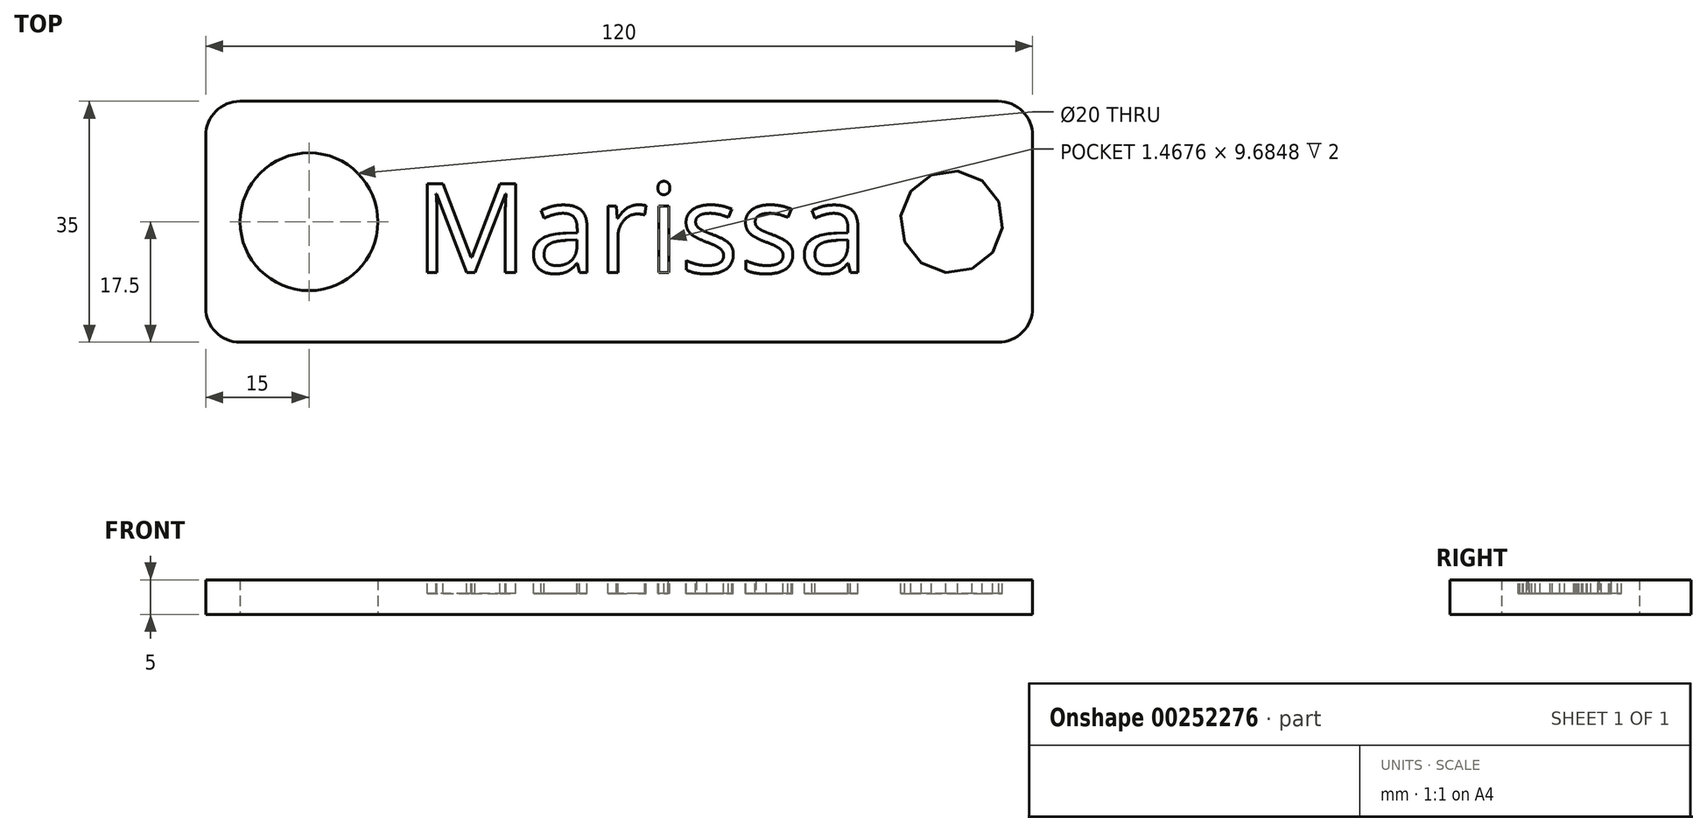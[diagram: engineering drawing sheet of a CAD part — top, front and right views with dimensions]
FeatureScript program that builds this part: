
annotation { "Feature Type Name" : "Feature", "Feature Type Description" : "" }
export const myFeature = defineFeature(function(context is Context, id is Id, definition is map)
    precondition{}
    {
        {
            var Q0;
            Q0=qCreatedBy(makeId("Top.planeOp"),FACE);
            var sketch = newSketch(context, id + "F0", { "sketchPlane" : qUnion([Q0])});
            skPoint(sketch, "E0.middle", {"position": v(0, 0) * mm});
            skLineSegment(sketch, "E1.bottom", {"start": v(60, -17.5) * mm, "end": v(-60, -17.5) * mm});
            skLineSegment(sketch, "E1.top", {"start": v(60, 17.5) * mm, "end": v(-60, 17.5) * mm});
            skLineSegment(sketch, "E1.left", {"start": v(60, -17.5) * mm, "end": v(60, 17.5) * mm});
            skLineSegment(sketch, "E1.right", {"start": v(-60, -17.5) * mm, "end": v(-60, 17.5) * mm});
            skCircle(sketch, "E2", {"center": v(-45, 0) * mm, "radius": 10 * mm});
            skSolve(sketch);
        }
        {
            var Q0;
            Q0=makeQuery(id+"F0.imprint","IMPRINT",FACE,{"disambiguationData":[TD([[makeQuery(id+"F0.imprint","IMPRINT",EDGE,{"derivedFrom":sQuery(id+"F0.wireOp",EDGE,"E1.bottom")}),-1.0]])]});
            extrude(context, id + "F1", {"entities" : qUnion([Q0]), "depth" : 5 * mm});
        }
        {
            var Q0;
            Q0=makeQuery(id+"F1.opExtrude","SWEPT_EDGE",EDGE,{"disambiguationData":[OSD([sQuery(id+"F0.wireOp",EDGE,"E1.bottom"),sQuery(id+"F0.wireOp",EDGE,"E1.right")])]});
            var Q1;
            Q1=makeQuery(id+"F1.opExtrude","SWEPT_EDGE",EDGE,{"disambiguationData":[OSD([sQuery(id+"F0.wireOp",EDGE,"E1.bottom"),sQuery(id+"F0.wireOp",EDGE,"E1.left")])]});
            var Q2;
            Q2=makeQuery(id+"F1.opExtrude","SWEPT_EDGE",EDGE,{"disambiguationData":[OSD([sQuery(id+"F0.wireOp",EDGE,"E1.top"),sQuery(id+"F0.wireOp",EDGE,"E1.left")])]});
            var Q3;
            Q3=makeQuery(id+"F1.opExtrude","SWEPT_EDGE",EDGE,{"disambiguationData":[OSD([sQuery(id+"F0.wireOp",EDGE,"E1.top"),sQuery(id+"F0.wireOp",EDGE,"E1.right")])]});
            fillet(context, id + "F2", {"entities" : qUnion([Q0, Q1, Q2, Q3]), "radius" : 5 * mm, "tangentPropagation" : true, "allowEdgeOverflow" : false});
        }
        {
            var Q0;
            Q0=makeQuery(id+"F1.opExtrude","CAP_FACE",FACE,{"disambiguationData":[OSD([sQuery(id+"F0.wireOp",EDGE,"E1.bottom"),sQuery(id+"F0.wireOp",EDGE,"E1.top"),sQuery(id+"F0.wireOp",EDGE,"E1.left"),sQuery(id+"F0.wireOp",EDGE,"E1.right"),sQuery(id+"F0.wireOp",EDGE,"E2")])],"isStart":false});
            var sketch = newSketch(context, id + "F3", { "sketchPlane" : qUnion([Q0])});
            skText(sketch, "E3", { "text": "Marissa", "fontName": "OpenSans-Regular.ttf"});
            skCircle(sketch, "E4.cCircle", {"center": v(48.26, 0) * mm, "radius": 7.17 * mm, "construction": true});
            skLineSegment(sketch, "E4.0", {"start": v(54.2, -4.44) * mm, "end": v(51.2, -6.81) * mm});
            skLineSegment(sketch, "E4.1", {"start": v(51.2, -6.81) * mm, "end": v(47.39, -7.37) * mm});
            skLineSegment(sketch, "E4.2", {"start": v(47.39, -7.37) * mm, "end": v(43.82, -5.95) * mm});
            skLineSegment(sketch, "E4.3", {"start": v(43.82, -5.95) * mm, "end": v(41.44, -2.93) * mm});
            skLineSegment(sketch, "E4.4", {"start": v(41.44, -2.93) * mm, "end": v(40.89, 0.87) * mm});
            skLineSegment(sketch, "E4.5", {"start": v(40.89, 0.87) * mm, "end": v(42.3, 4.44) * mm});
            skLineSegment(sketch, "E4.6", {"start": v(42.3, 4.44) * mm, "end": v(45.32, 6.81) * mm});
            skLineSegment(sketch, "E4.7", {"start": v(45.32, 6.81) * mm, "end": v(49.12, 7.37) * mm});
            skLineSegment(sketch, "E4.8", {"start": v(49.12, 7.37) * mm, "end": v(52.7, 5.95) * mm});
            skLineSegment(sketch, "E4.9", {"start": v(52.7, 5.95) * mm, "end": v(55.07, 2.93) * mm});
            skLineSegment(sketch, "E4.10", {"start": v(55.07, 2.93) * mm, "end": v(55.63, -0.87) * mm});
            skLineSegment(sketch, "E4.11", {"start": v(55.63, -0.87) * mm, "end": v(54.2, -4.44) * mm});
            skPoint(sketch, "E4.0.midPoint", {"position": v(52.7, -5.63) * mm});
            const initialGuessF3  = {"E3": [-0.0296, -0.0074, 1, 0, 0.01303]};
            skSetInitialGuess(sketch, initialGuessF3);
            skSolve(sketch);
        }
        {
            var Q0;
            Q0 = qSketchRegion(id + "F3", true);
            extrude(context, id + "F4", {"entities" : qUnion([Q0]), "operationType" : NewBodyOperationType.REMOVE, "depth" : 4.7 * mm});
        }
        {
            var Q0;
            Q0 = qSketchRegion(id + "F3", true);
            extrude(context, id + "F5", {"entities" : qUnion([Q0]), "operationType" : NewBodyOperationType.REMOVE, "oppositeDirection" : true, "depth" : 2 * mm});
        }
    });
